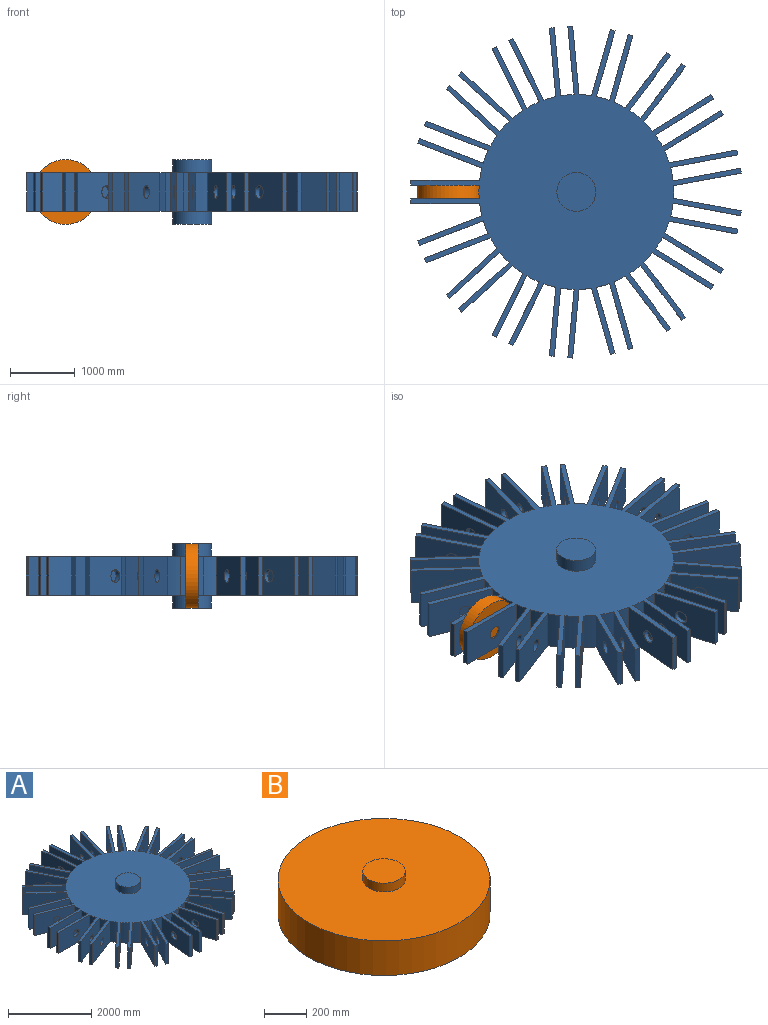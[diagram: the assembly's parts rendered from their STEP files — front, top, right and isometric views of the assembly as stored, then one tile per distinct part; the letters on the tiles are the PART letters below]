
ASSEMBLY  parts=2 mates=1
PART A: 176 faces, bbox 5089.7x5111.5x1000 mm
  f0: plane 982.53x600mm, normal (-0.36,-0.93,0), area 600791.8mm2, adj f5,f6,f7,f8,f175
  f1: plane 982.53x600mm, normal (0.36,0.93,0), area 600791.8mm2, adj f4,f6,f7,f9,f175
  f2: plane 989.2x600mm, normal (-0.36,-0.93,0), area 605087.6mm2, adj f4,f6,f7,f9,f144
  f3: plane 989.2x600mm, normal (0.36,0.93,0), area 605087.6mm2, adj f5,f6,f7,f8,f174
  f4: plane 600x69.94mm, normal (-0.93,0.36,0), area 45000mm2, adj f1,f2,f6,f7
  f5: plane 600x69.94mm, normal (-0.93,0.36,0), area 45000mm2, adj f0,f3,f6,f7
  f6: plane 5111.46x5089.66mm, normal (0,0,-1), area 9481043.5mm2, adj f0,f1,f2,f3,f4,f5,f11,f12
  f7: plane 5111.46x5089.66mm, normal (0,0,1), area 9481043.5mm2, adj f0,f1,f2,f3,f4,f5,f11,f12
  f8: cylinder r=100mm len=213.59mm, axis (-0.36,-0.93,0), area 47123.9mm2, adj f0,f3
  f9: cylinder r=100mm len=213.59mm, axis (-0.36,-0.93,0), area 47123.9mm2, adj f1,f2
  f10: cylinder r=100mm len=212.46mm, axis (-0.9,-0.45,0), area 47123.9mm2, adj f12,f13
  f11: plane 600x67.14mm, normal (-0.45,0.9,0), area 45000mm2, adj f6,f7,f12,f13
  f12: plane 949.62x600mm, normal (0.9,0.45,0), area 605087.6mm2, adj f6,f7,f10,f11,f172
  f13: plane 943.22x600mm, normal (-0.9,-0.45,0), area 600791.8mm2, adj f6,f7,f10,f11,f173
  f14: plane 943.22x600mm, normal (0.9,0.45,0), area 600791.8mm2, adj f6,f7,f16,f17,f173
  f15: plane 949.62x600mm, normal (-0.9,-0.45,0), area 605087.6mm2, adj f6,f7,f16,f17,f131
  f16: plane 600x67.14mm, normal (-0.45,0.9,0), area 45000mm2, adj f6,f7,f14,f15
  f17: cylinder r=100mm len=212.46mm, axis (-0.9,-0.45,0), area 47123.9mm2, adj f14,f15
  f18: cylinder r=100mm len=206.07mm, axis (-1,-0.09,0), area 47123.9mm2, adj f20,f21
  f19: plane 600x74.68mm, normal (-0.09,1,0), area 45000mm2, adj f6,f7,f20,f21
  f20: plane 1056.31x600mm, normal (-1,-0.09,0), area 605087.6mm2, adj f6,f7,f18,f19,f172
  f21: plane 1049.18x600mm, normal (1,0.09,0), area 600791.8mm2, adj f6,f7,f18,f19,f171
  f22: plane 1056.31x600mm, normal (1,0.09,0), area 605087.6mm2, adj f6,f7,f24,f25,f170
  f23: plane 1049.18x600mm, normal (-1,-0.09,0), area 600791.8mm2, adj f6,f7,f24,f25,f171
  f24: cylinder r=100mm len=206.07mm, axis (-1,-0.09,0), area 47123.9mm2, adj f22,f23
  f25: plane 600x74.68mm, normal (-0.09,1,0), area 45000mm2, adj f6,f7,f22,f23
  f26: cylinder r=100mm len=212.89mm, axis (-0.96,0.27,0), area 47123.9mm2, adj f28,f29
  f27: plane 600x72.14mm, normal (0.27,0.96,0), area 45000mm2, adj f6,f7,f28,f29
  f28: plane 1020.34x600mm, normal (-0.96,0.27,0), area 605087.6mm2, adj f6,f7,f26,f27,f170
  f29: plane 1013.46x600mm, normal (0.96,-0.27,0), area 600791.8mm2, adj f6,f7,f26,f27,f169
  f30: plane 1020.34x600mm, normal (0.96,-0.27,0), area 605087.6mm2, adj f6,f7,f32,f33,f168
  f31: plane 1013.46x600mm, normal (-0.96,0.27,0), area 600791.8mm2, adj f6,f7,f32,f33,f169
  f32: cylinder r=100mm len=212.89mm, axis (-0.96,0.27,0), area 47123.9mm2, adj f30,f31
  f33: plane 600x72.14mm, normal (0.27,0.96,0), area 45000mm2, adj f6,f7,f30,f31
  f34: cylinder r=100mm len=204.8mm, axis (-0.8,0.6,0), area 47123.9mm2, adj f36,f37
  f35: plane 600x59.85mm, normal (0.6,0.8,0), area 45000mm2, adj f6,f7,f36,f37
  f36: plane 846.57x639.3mm, normal (-0.8,0.6,0), area 605087.6mm2, adj f6,f7,f34,f35,f168
  f37: plane 840.85x634.98mm, normal (0.8,-0.6,0), area 600791.8mm2, adj f6,f7,f34,f35,f167
  f38: plane 846.57x639.3mm, normal (0.8,-0.6,0), area 605087.6mm2, adj f6,f7,f40,f41,f166
  f39: plane 840.85x634.98mm, normal (-0.8,0.6,0), area 600791.8mm2, adj f6,f7,f40,f41,f167
  f40: cylinder r=100mm len=204.8mm, axis (-0.8,0.6,0), area 47123.9mm2, adj f38,f39
  f41: plane 600x59.85mm, normal (0.6,0.8,0), area 45000mm2, adj f6,f7,f38,f39
  f42: cylinder r=100mm len=209.53mm, axis (-0.53,0.85,0), area 47123.9mm2, adj f44,f45
  f43: plane 600x63.77mm, normal (0.85,0.53,0), area 45000mm2, adj f6,f7,f44,f45
  f44: plane 901.94x600mm, normal (-0.53,0.85,0), area 605087.6mm2, adj f6,f7,f42,f43,f166
  f45: plane 895.86x600mm, normal (0.53,-0.85,0), area 600791.8mm2, adj f6,f7,f42,f43,f165
  f46: plane 901.94x600mm, normal (0.53,-0.85,0), area 605087.6mm2, adj f6,f7,f48,f49,f164
  f47: plane 895.86x600mm, normal (-0.53,0.85,0), area 600791.8mm2, adj f6,f7,f48,f49,f165
  f48: cylinder r=100mm len=209.53mm, axis (-0.53,0.85,0), area 47123.9mm2, adj f46,f47
  f49: plane 600x63.77mm, normal (0.85,0.53,0), area 45000mm2, adj f6,f7,f46,f47
  f50: cylinder r=100mm len=210.38mm, axis (-0.18,0.98,0), area 47123.9mm2, adj f52,f53
  f51: plane 600x73.72mm, normal (0.98,0.18,0), area 45000mm2, adj f6,f7,f52,f53
  f52: plane 1042.78x600mm, normal (-0.18,0.98,0), area 605087.6mm2, adj f6,f7,f50,f51,f164
  f53: plane 1035.74x600mm, normal (0.18,-0.98,0), area 600791.8mm2, adj f6,f7,f50,f51,f163
  f54: plane 1042.78x600mm, normal (0.18,-0.98,0), area 605087.6mm2, adj f6,f7,f56,f57,f162
  f55: plane 1035.74x600mm, normal (-0.18,0.98,0), area 600791.8mm2, adj f6,f7,f56,f57,f163
  f56: cylinder r=100mm len=210.38mm, axis (-0.18,0.98,0), area 47123.9mm2, adj f54,f55
  f57: plane 600x73.72mm, normal (0.98,0.18,0), area 45000mm2, adj f6,f7,f54,f55
  f58: cylinder r=100mm len=210.38mm, axis (0.18,0.98,0), area 47123.9mm2, adj f60,f61
  f59: plane 600x73.72mm, normal (0.98,-0.18,0), area 45000mm2, adj f6,f7,f60,f61
  f60: plane 1042.78x600mm, normal (0.18,0.98,0), area 605087.6mm2, adj f6,f7,f58,f59,f162
  f61: plane 1035.74x600mm, normal (-0.18,-0.98,0), area 600791.8mm2, adj f6,f7,f58,f59,f161
  f62: plane 1042.78x600mm, normal (-0.18,-0.98,0), area 605087.6mm2, adj f6,f7,f64,f65,f160
  f63: plane 1035.74x600mm, normal (0.18,0.98,0), area 600791.8mm2, adj f6,f7,f64,f65,f161
  f64: cylinder r=100mm len=210.38mm, axis (0.18,0.98,0), area 47123.9mm2, adj f62,f63
  f65: plane 600x73.72mm, normal (0.98,-0.18,0), area 45000mm2, adj f6,f7,f62,f63
  f66: cylinder r=100mm len=209.53mm, axis (0.53,0.85,0), area 47123.9mm2, adj f68,f69
  f67: plane 600x63.77mm, normal (0.85,-0.53,0), area 45000mm2, adj f6,f7,f68,f69
  f68: plane 901.94x600mm, normal (0.53,0.85,0), area 605087.6mm2, adj f6,f7,f66,f67,f160
  f69: plane 895.86x600mm, normal (-0.53,-0.85,0), area 600791.8mm2, adj f6,f7,f66,f67,f159
  f70: plane 901.94x600mm, normal (-0.53,-0.85,0), area 605087.6mm2, adj f6,f7,f72,f73,f158
  f71: plane 895.86x600mm, normal (0.53,0.85,0), area 600791.8mm2, adj f6,f7,f72,f73,f159
  f72: cylinder r=100mm len=209.53mm, axis (0.53,0.85,0), area 47123.9mm2, adj f70,f71
  f73: plane 600x63.77mm, normal (0.85,-0.53,0), area 45000mm2, adj f6,f7,f70,f71
  f74: cylinder r=100mm len=204.8mm, axis (0.8,0.6,0), area 47123.9mm2, adj f76,f77
  f75: plane 600x59.85mm, normal (0.6,-0.8,0), area 45000mm2, adj f6,f7,f76,f77
  f76: plane 846.57x639.3mm, normal (0.8,0.6,0), area 605087.6mm2, adj f6,f7,f74,f75,f158
  f77: plane 840.85x634.98mm, normal (-0.8,-0.6,0), area 600791.8mm2, adj f6,f7,f74,f75,f157
  f78: plane 846.57x639.3mm, normal (-0.8,-0.6,0), area 605087.6mm2, adj f6,f7,f80,f81,f156
  f79: plane 840.85x634.98mm, normal (0.8,0.6,0), area 600791.8mm2, adj f6,f7,f80,f81,f157
  f80: cylinder r=100mm len=204.8mm, axis (0.8,0.6,0), area 47123.9mm2, adj f78,f79
  f81: plane 600x59.85mm, normal (0.6,-0.8,0), area 45000mm2, adj f6,f7,f78,f79
  f82: cylinder r=100mm len=212.89mm, axis (0.96,0.27,0), area 47123.9mm2, adj f84,f85
  f83: plane 600x72.14mm, normal (0.27,-0.96,0), area 45000mm2, adj f6,f7,f84,f85
  f84: plane 1020.34x600mm, normal (0.96,0.27,0), area 605087.6mm2, adj f6,f7,f82,f83,f156
  f85: plane 1013.46x600mm, normal (-0.96,-0.27,0), area 600791.8mm2, adj f6,f7,f82,f83,f155
  f86: plane 1020.34x600mm, normal (-0.96,-0.27,0), area 605087.6mm2, adj f6,f7,f88,f89,f154
  f87: plane 1013.46x600mm, normal (0.96,0.27,0), area 600791.8mm2, adj f6,f7,f88,f89,f155
  f88: cylinder r=100mm len=212.89mm, axis (0.96,0.27,0), area 47123.9mm2, adj f86,f87
  f89: plane 600x72.14mm, normal (0.27,-0.96,0), area 45000mm2, adj f6,f7,f86,f87
  f90: cylinder r=100mm len=206.07mm, axis (1,-0.09,0), area 47123.9mm2, adj f92,f93
  f91: plane 600x74.68mm, normal (-0.09,-1,0), area 45000mm2, adj f6,f7,f92,f93
  f92: plane 1056.31x600mm, normal (1,-0.09,0), area 605087.6mm2, adj f6,f7,f90,f91,f154
  f93: plane 1049.18x600mm, normal (-1,0.09,0), area 600791.8mm2, adj f6,f7,f90,f91,f153
  f94: plane 1056.31x600mm, normal (-1,0.09,0), area 605087.6mm2, adj f6,f7,f96,f97,f152
  f95: plane 1049.18x600mm, normal (1,-0.09,0), area 600791.8mm2, adj f6,f7,f96,f97,f153
  f96: cylinder r=100mm len=206.07mm, axis (1,-0.09,0), area 47123.9mm2, adj f94,f95
  f97: plane 600x74.68mm, normal (-0.09,-1,0), area 45000mm2, adj f6,f7,f94,f95
  f98: cylinder r=100mm len=212.46mm, axis (0.9,-0.45,0), area 47123.9mm2, adj f100,f101
  f99: plane 600x67.14mm, normal (-0.45,-0.9,0), area 45000mm2, adj f6,f7,f100,f101
  f100: plane 949.62x600mm, normal (0.9,-0.45,0), area 605087.6mm2, adj f6,f7,f98,f99,f152
  f101: plane 943.22x600mm, normal (-0.9,0.45,0), area 600791.8mm2, adj f6,f7,f98,f99,f151
  f102: plane 949.62x600mm, normal (-0.9,0.45,0), area 605087.6mm2, adj f6,f7,f104,f105,f150
  f103: plane 943.22x600mm, normal (0.9,-0.45,0), area 600791.8mm2, adj f6,f7,f104,f105,f151
  f104: cylinder r=100mm len=212.46mm, axis (0.9,-0.45,0), area 47123.9mm2, adj f102,f103
  f105: plane 600x67.14mm, normal (-0.45,-0.9,0), area 45000mm2, adj f6,f7,f102,f103
  f106: cylinder r=100mm len=200mm, axis (0.67,-0.74,0), area 47123.9mm2, adj f108,f109
  f107: plane 600x55.43mm, normal (-0.74,-0.67,0), area 45000mm2, adj f6,f7,f108,f109
  f108: plane 783.97x714.68mm, normal (0.67,-0.74,0), area 605087.6mm2, adj f6,f7,f106,f107,f150
  f109: plane 778.68x709.86mm, normal (-0.67,0.74,0), area 600791.8mm2, adj f6,f7,f106,f107,f149
  f110: plane 783.97x714.68mm, normal (-0.67,0.74,0), area 605087.6mm2, adj f6,f7,f112,f113,f148
  f111: plane 778.68x709.86mm, normal (0.67,-0.74,0), area 600791.8mm2, adj f6,f7,f112,f113,f149
  f112: cylinder r=100mm len=200mm, axis (0.67,-0.74,0), area 47123.9mm2, adj f110,f111
  f113: plane 600x55.43mm, normal (-0.74,-0.67,0), area 45000mm2, adj f6,f7,f110,f111
  f114: cylinder r=100mm len=213.59mm, axis (0.36,-0.93,0), area 47123.9mm2, adj f116,f117
  f115: plane 600x69.94mm, normal (-0.93,-0.36,0), area 45000mm2, adj f6,f7,f116,f117
  f116: plane 989.2x600mm, normal (0.36,-0.93,0), area 605087.6mm2, adj f6,f7,f114,f115,f148
  f117: plane 982.53x600mm, normal (-0.36,0.93,0), area 600791.8mm2, adj f6,f7,f114,f115,f147
  f118: plane 989.2x600mm, normal (-0.36,0.93,0), area 605087.6mm2, adj f6,f7,f120,f121,f146
  f119: plane 982.53x600mm, normal (0.36,-0.93,0), area 600791.8mm2, adj f6,f7,f120,f121,f147
  f120: cylinder r=100mm len=213.59mm, axis (0.36,-0.93,0), area 47123.9mm2, adj f118,f119
  f121: plane 600x69.94mm, normal (-0.93,-0.36,0), area 45000mm2, adj f6,f7,f118,f119
  f122: cylinder r=100mm len=200mm, axis (0,-1,0), area 47123.9mm2, adj f124,f125
  f123: plane 600x75mm, normal (-1,0,0), area 45000mm2, adj f6,f7,f124,f125
  f124: plane 1060.84x600mm, normal (0,-1,0), area 605087.6mm2, adj f6,f7,f122,f123,f146
  f125: plane 1053.68x600mm, normal (0,1,0), area 600791.8mm2, adj f6,f7,f122,f123,f145
  f126: plane 1060.84x600mm, normal (0,1,0), area 605087.6mm2, adj f6,f7,f128,f129,f144
  f127: plane 1053.68x600mm, normal (0,-1,0), area 600791.8mm2, adj f6,f7,f128,f129,f145
  f128: cylinder r=100mm len=200mm, axis (0,-1,0), area 47123.9mm2, adj f126,f127
  f129: plane 600x75mm, normal (-1,0,0), area 45000mm2, adj f6,f7,f126,f127
  f130: cylinder r=1500mm len=600mm, axis (0,0,-1), area 126103.1mm2, adj f6,f7,f142,f143
  f131: cylinder r=1500mm len=600mm, axis (0,0,-1), area 116117.4mm2, adj f6,f7,f15,f140
  f132: plane 600x600mm, normal (0,0,-1), area 282743.3mm2, adj f133
  f133: cylinder r=300mm len=600mm, axis (0,0,-1), area 376991.1mm2, adj f6,f132
  f134: cylinder r=300mm len=600mm, axis (0,0,-1), area 376991.1mm2, adj f7,f135
  f135: plane 600x600mm, normal (0,0,1), area 282743.3mm2, adj f134
  f136: cylinder r=100mm len=200mm, axis (-0.67,-0.74,0), area 47123.9mm2, adj f141,f142
  f137: cylinder r=100mm len=200mm, axis (-0.67,-0.74,0), area 47123.9mm2, adj f140,f143
  f138: plane 600x55.43mm, normal (-0.74,0.67,0), area 45000mm2, adj f6,f7,f140,f143
  f139: plane 600x55.43mm, normal (-0.74,0.67,0), area 45000mm2, adj f6,f7,f141,f142
  f140: plane 783.97x714.68mm, normal (0.67,0.74,0), area 605087.6mm2, adj f6,f7,f131,f137,f138
  f141: plane 783.97x714.68mm, normal (-0.67,-0.74,0), area 605087.6mm2, adj f6,f7,f136,f139,f174
  f142: plane 778.68x709.86mm, normal (0.67,0.74,0), area 600791.8mm2, adj f6,f7,f130,f136,f139
  f143: plane 778.68x709.86mm, normal (-0.67,-0.74,0), area 600791.8mm2, adj f6,f7,f130,f137,f138
  f144: cylinder r=1500mm len=600mm, axis (0,0,-1), area 116117.4mm2, adj f2,f6,f7,f126
  f145: cylinder r=1500mm len=600mm, axis (0,0,-1), area 126103.1mm2, adj f6,f7,f125,f127
  f146: cylinder r=1500mm len=600mm, axis (0,0,-1), area 116117.4mm2, adj f6,f7,f118,f124
  f147: cylinder r=1500mm len=600mm, axis (0,0,-1), area 126103.1mm2, adj f6,f7,f117,f119
  f148: cylinder r=1500mm len=600mm, axis (0,0,-1), area 116117.4mm2, adj f6,f7,f110,f116
  f149: cylinder r=1500mm len=600mm, axis (0,0,-1), area 126103.1mm2, adj f6,f7,f109,f111
  f150: cylinder r=1500mm len=600mm, axis (0,0,-1), area 116117.4mm2, adj f6,f7,f102,f108
  f151: cylinder r=1500mm len=600mm, axis (0,0,-1), area 126103.1mm2, adj f6,f7,f101,f103
  f152: cylinder r=1500mm len=600mm, axis (0,0,-1), area 116117.4mm2, adj f6,f7,f94,f100
  f153: cylinder r=1500mm len=600mm, axis (0,0,-1), area 126103.1mm2, adj f6,f7,f93,f95
  f154: cylinder r=1500mm len=600mm, axis (0,0,-1), area 116117.4mm2, adj f6,f7,f86,f92
  f155: cylinder r=1500mm len=600mm, axis (0,0,-1), area 126103.1mm2, adj f6,f7,f85,f87
  f156: cylinder r=1500mm len=600mm, axis (0,0,-1), area 116117.4mm2, adj f6,f7,f78,f84
  f157: cylinder r=1500mm len=600mm, axis (0,0,-1), area 126103.1mm2, adj f6,f7,f77,f79
  f158: cylinder r=1500mm len=600mm, axis (0,0,-1), area 116117.4mm2, adj f6,f7,f70,f76
  f159: cylinder r=1500mm len=600mm, axis (0,0,-1), area 126103.1mm2, adj f6,f7,f69,f71
  f160: cylinder r=1500mm len=600mm, axis (0,0,-1), area 116117.4mm2, adj f6,f7,f62,f68
  f161: cylinder r=1500mm len=600mm, axis (0,0,-1), area 126103.1mm2, adj f6,f7,f61,f63
  f162: cylinder r=1500mm len=600mm, axis (0,0,-1), area 116117.4mm2, adj f6,f7,f54,f60
  f163: cylinder r=1500mm len=600mm, axis (0,0,-1), area 126103.1mm2, adj f6,f7,f53,f55
  f164: cylinder r=1500mm len=600mm, axis (0,0,-1), area 116117.4mm2, adj f6,f7,f46,f52
  f165: cylinder r=1500mm len=600mm, axis (0,0,-1), area 126103.1mm2, adj f6,f7,f45,f47
  f166: cylinder r=1500mm len=600mm, axis (0,0,-1), area 116117.4mm2, adj f6,f7,f38,f44
  f167: cylinder r=1500mm len=600mm, axis (0,0,-1), area 126103.1mm2, adj f6,f7,f37,f39
  f168: cylinder r=1500mm len=600mm, axis (0,0,-1), area 116117.4mm2, adj f6,f7,f30,f36
  f169: cylinder r=1500mm len=600mm, axis (0,0,-1), area 126103.1mm2, adj f6,f7,f29,f31
  f170: cylinder r=1500mm len=600mm, axis (0,0,-1), area 116117.4mm2, adj f6,f7,f22,f28
  f171: cylinder r=1500mm len=600mm, axis (0,0,-1), area 126103.1mm2, adj f6,f7,f21,f23
  f172: cylinder r=1500mm len=600mm, axis (0,0,-1), area 116117.4mm2, adj f6,f7,f12,f20
  f173: cylinder r=1500mm len=600mm, axis (0,0,-1), area 126103.1mm2, adj f6,f7,f13,f14
  f174: cylinder r=1500mm len=600mm, axis (0,0,-1), area 116117.4mm2, adj f3,f6,f7,f141
  f175: cylinder r=1500mm len=600mm, axis (0,0,-1), area 126103.1mm2, adj f0,f1,f6,f7
PART B: 7 faces, bbox 1000x1000x300 mm
  f0: cylinder r=500mm len=1000mm, axis (0,0,-1), area 628318.5mm2, adj f1,f2
  f1: plane 1000x1000mm, normal (0,0,1), area 753982.2mm2, adj f0,f5
  f2: plane 1000x1000mm, normal (0,0,-1), area 753982.2mm2, adj f0,f4
  f3: plane 200x200mm, normal (0,0,-1), area 31415.9mm2, adj f4
  f4: cylinder r=100mm len=200mm, axis (0,0,-1), area 31415.9mm2, adj f2,f3
  f5: cylinder r=100mm len=200mm, axis (0,0,-1), area 31415.9mm2, adj f1,f6
  f6: plane 200x200mm, normal (0,0,1), area 31415.9mm2, adj f5
PLACE A at identity fixed
PLACE B rot(axis=(1,0,0),90deg) t=(-1950,0,0)mm
MATE revolute A.f122 <-> B.f0  axis (0,1,0) through (-1950,0,0)mm
